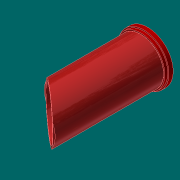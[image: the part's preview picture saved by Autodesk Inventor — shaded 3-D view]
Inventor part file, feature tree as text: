
AUTODESK INVENTOR PART (.ipt)
format: ipt  version: 2017.3 (Build 213257000, 257)  size: 139,264 bytes
history: native  units: in
note: dims shown in document units (in); Inventor stores cm internally (conversion verified against a paired STEP export)
features: other x3, extrude x2, sketch x2
ambient origin geometry x8: Origin, YZ Plane, XZ Plane, XY Plane, X Axis, Y Axis, Z Axis, Center Point
bodies: Solid1 (feature_tree)
feature tree (7):
  other  "A1-19010-100-02 HCWI nozzle insert.ipt"
  extrude  "Extrusion1"  Depth=0.5in
  extrude  "Extrusion2"  Depth=0.5in TaperAngle=0.0deg
  other  "Solid1::A1-19010-100-02 HCWI nozzle insert.ipt"
  other  "TaggingFeature1"
  sketch  "Sketch2"  dims[d0=0.3937in]
  sketch  "Sketch3"  dims[d1=2.0in d2=0.0in d3=28.52in d4=3.75in d5=0.0in d6=27.5in d7=68.7402in d8=0.0in d9=25.0in d12=0.0in d13=0.0312in d16=0.0312in d17=0.0312in d18=0.2749in d20=0.0in d24=0.25in d10=30.5118in d11=0.5in d14=2.0in d15=0.0in d19=0.0in d21=29.0157in d22=0.5in d23=0.0in]
